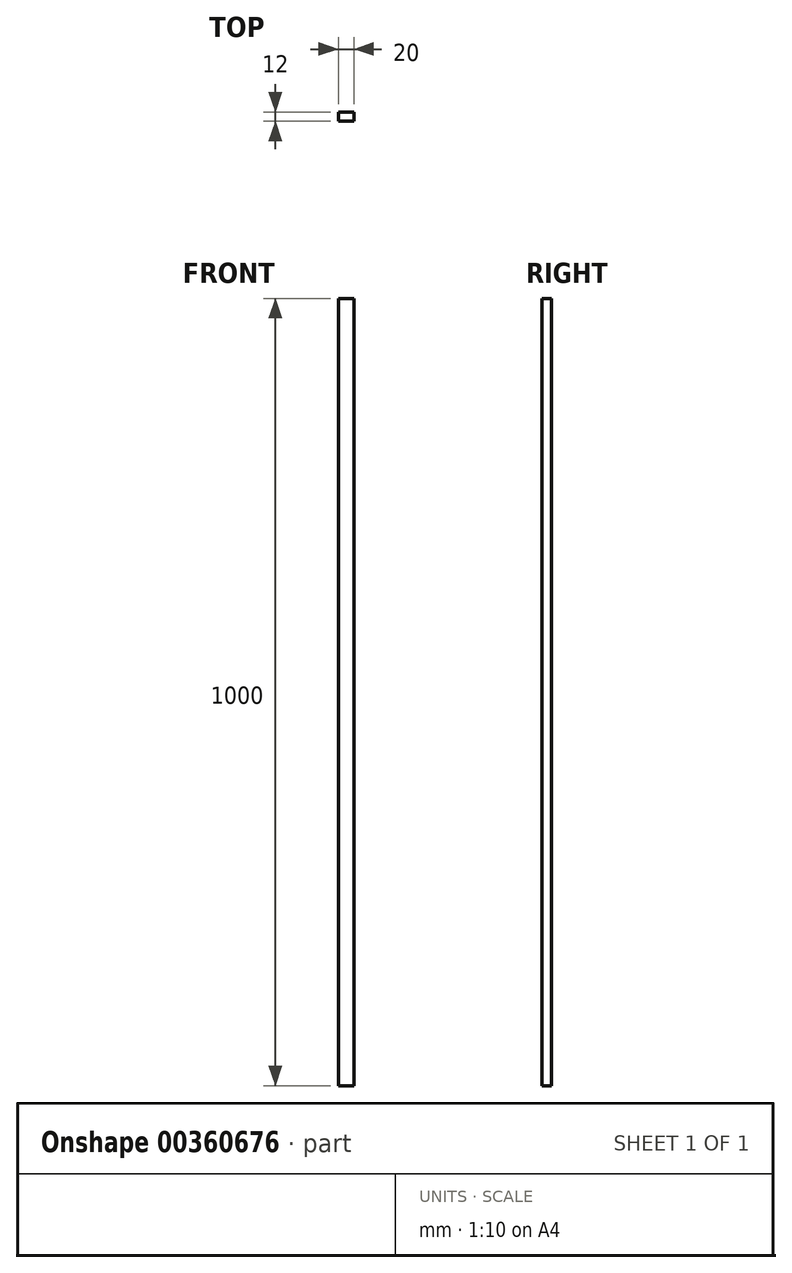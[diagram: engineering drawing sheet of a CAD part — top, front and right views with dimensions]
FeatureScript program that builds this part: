
annotation { "Feature Type Name" : "Feature", "Feature Type Description" : "" }
export const myFeature = defineFeature(function(context is Context, id is Id, definition is map)
    precondition{}
    {
        {
            var Q0;
            Q0=qCreatedBy(makeId("Front.planeOp"),FACE);
            var sketch = newSketch(context, id + "F0", { "sketchPlane" : qUnion([Q0])});
            skLineSegment(sketch, "E0.bottom", {"start": v(0, 0) * mm, "end": v(20, 0) * mm});
            skLineSegment(sketch, "E0.top", {"start": v(0, 1000) * mm, "end": v(20, 1000) * mm});
            skLineSegment(sketch, "E0.left", {"start": v(0, 0) * mm, "end": v(0, 1000) * mm});
            skLineSegment(sketch, "E0.right", {"start": v(20, 0) * mm, "end": v(20, 1000) * mm});
            skSolve(sketch);
        }
        {
            var Q0;
            Q0=makeQuery(id+"F0.imprint","IMPRINT",FACE,{"disambiguationData":[TD([[makeQuery(id+"F0.imprint","IMPRINT",EDGE,{"derivedFrom":sQuery(id+"F0.wireOp",EDGE,"E0.bottom")}),1.0]])]});
            extrude(context, id + "F1", {"entities" : qUnion([Q0]), "depth" : 12 * mm});
        }
    });
